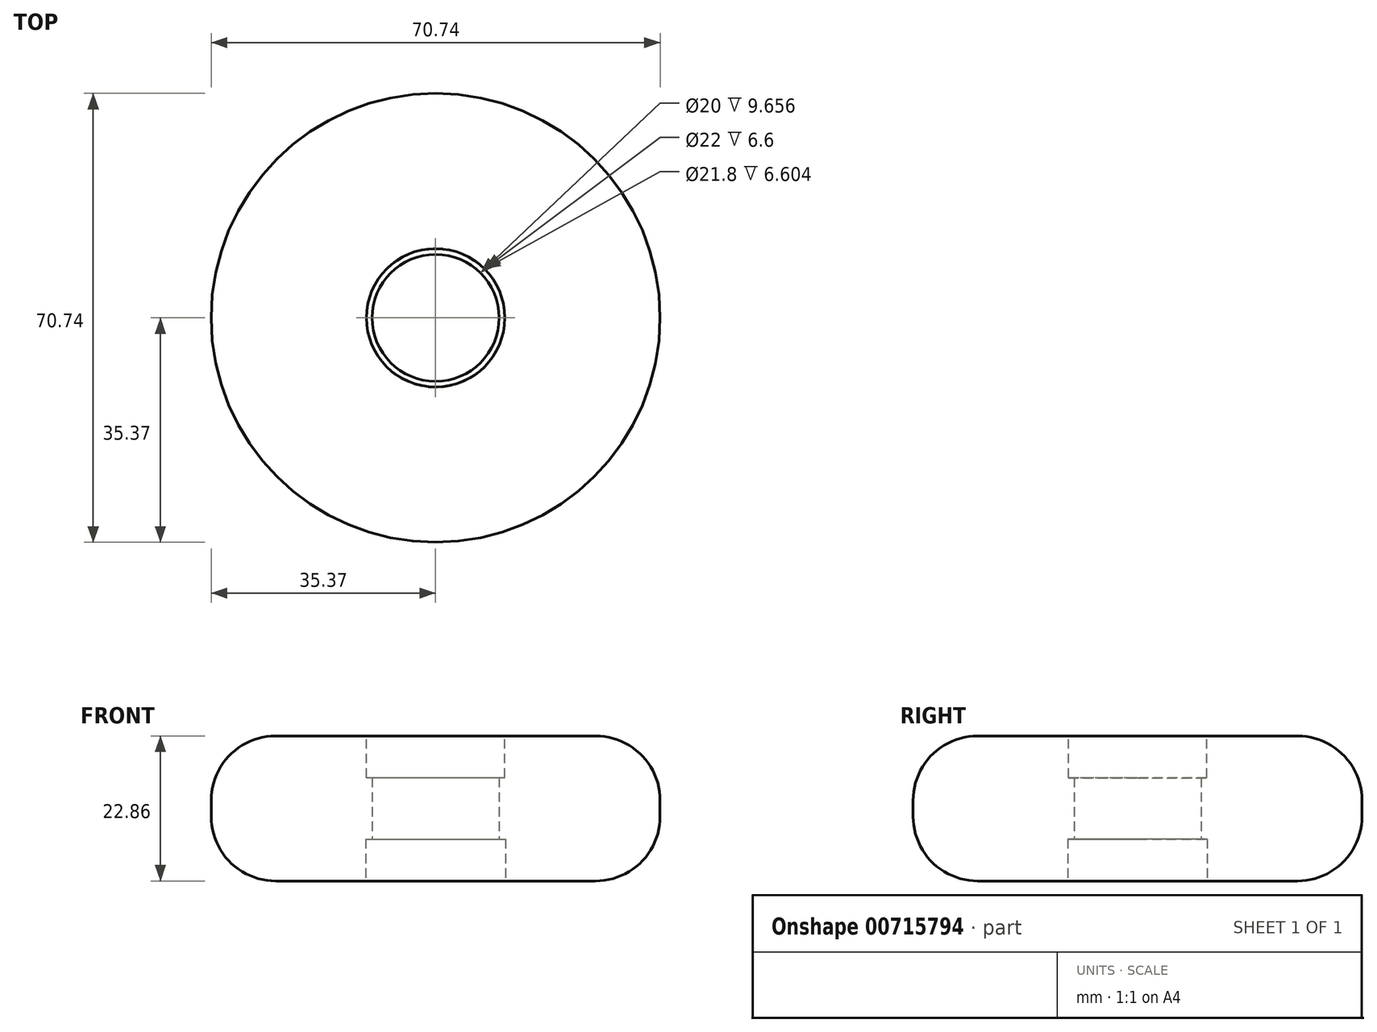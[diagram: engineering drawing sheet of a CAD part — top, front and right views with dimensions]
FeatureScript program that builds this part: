
annotation { "Feature Type Name" : "Feature", "Feature Type Description" : "" }
export const myFeature = defineFeature(function(context is Context, id is Id, definition is map)
    precondition{}
    {
        {
            var Q0;
            Q0=qCreatedBy(makeId("Top.planeOp"),FACE);
            var sketch = newSketch(context, id + "F0", { "sketchPlane" : qUnion([Q0])});
            skCircle(sketch, "E0", {"center": v(0, 0) * mm, "radius": 35.37 * mm});
            skSolve(sketch);
        }
        {
            var Q0;
            Q0 = qSketchRegion(id + "F0", true);
            extrude(context, id + "F1", {"entities" : qUnion([Q0]), "depth" : 22.86 * mm, "offsetDistance" : 25.4 * mm});
        }
        {
            var Q0;
            Q0=sQuery(id+"F0.wireOp",VERTEX,"E0.center");
            var Q1;
            Q1=makeQuery(id+"F1.opExtrude","SWEPT_BODY",BODY,{"disambiguationData":[OSD([sQuery(id+"F0.wireOp",EDGE,"E0")])]});
            hole(context, id + "F2", {"style" : HoleStyle.C_BORE, "endStyle" : HoleEndStyle.THROUGH, "oppositeDirection" : true, "holeDiameter" : 20 * mm, "cBoreDiameter" : 22 * mm, "cBoreDepth" : 6.6 * mm, "majorDiameter" : 6.35 * mm, "isTappedThrough" : true, "tappedDepth" : 12.7 * mm, "tapClearance" : 3, "locations" : qUnion([Q0]), "scope" : qUnion([Q1])});
        }
        {
            var Q0;
            Q0=makeQuery(id+"F1.opExtrude","CAP_FACE",FACE,{"disambiguationData":[OSD([sQuery(id+"F0.wireOp",EDGE,"E0")])],"isStart":false});
            var sketch = newSketch(context, id + "F3", { "sketchPlane" : qUnion([Q0])});
            skCircle(sketch, "E1", {"center": v(0, 0) * mm, "radius": 10.9 * mm});
            skSolve(sketch);
        }
        {
            var Q0;
            Q0 = qSketchRegion(id + "F3", true);
            extrude(context, id + "F4", {"entities" : qUnion([Q0]), "operationType" : NewBodyOperationType.REMOVE, "oppositeDirection" : true, "depth" : 6.6 * mm, "offsetDistance" : 25.4 * mm});
        }
        {
            var Q0;
            Q0=makeQuery(id+"F1.opExtrude","SWEPT_FACE",FACE,{"disambiguationData":[OSD([sQuery(id+"F0.wireOp",EDGE,"E0")])]});
            fillet(context, id + "F5", {"entities" : qUnion([Q0]), "radius" : 10.16 * mm, "tangentPropagation" : true, "allowEdgeOverflow" : false});
        }
    });
